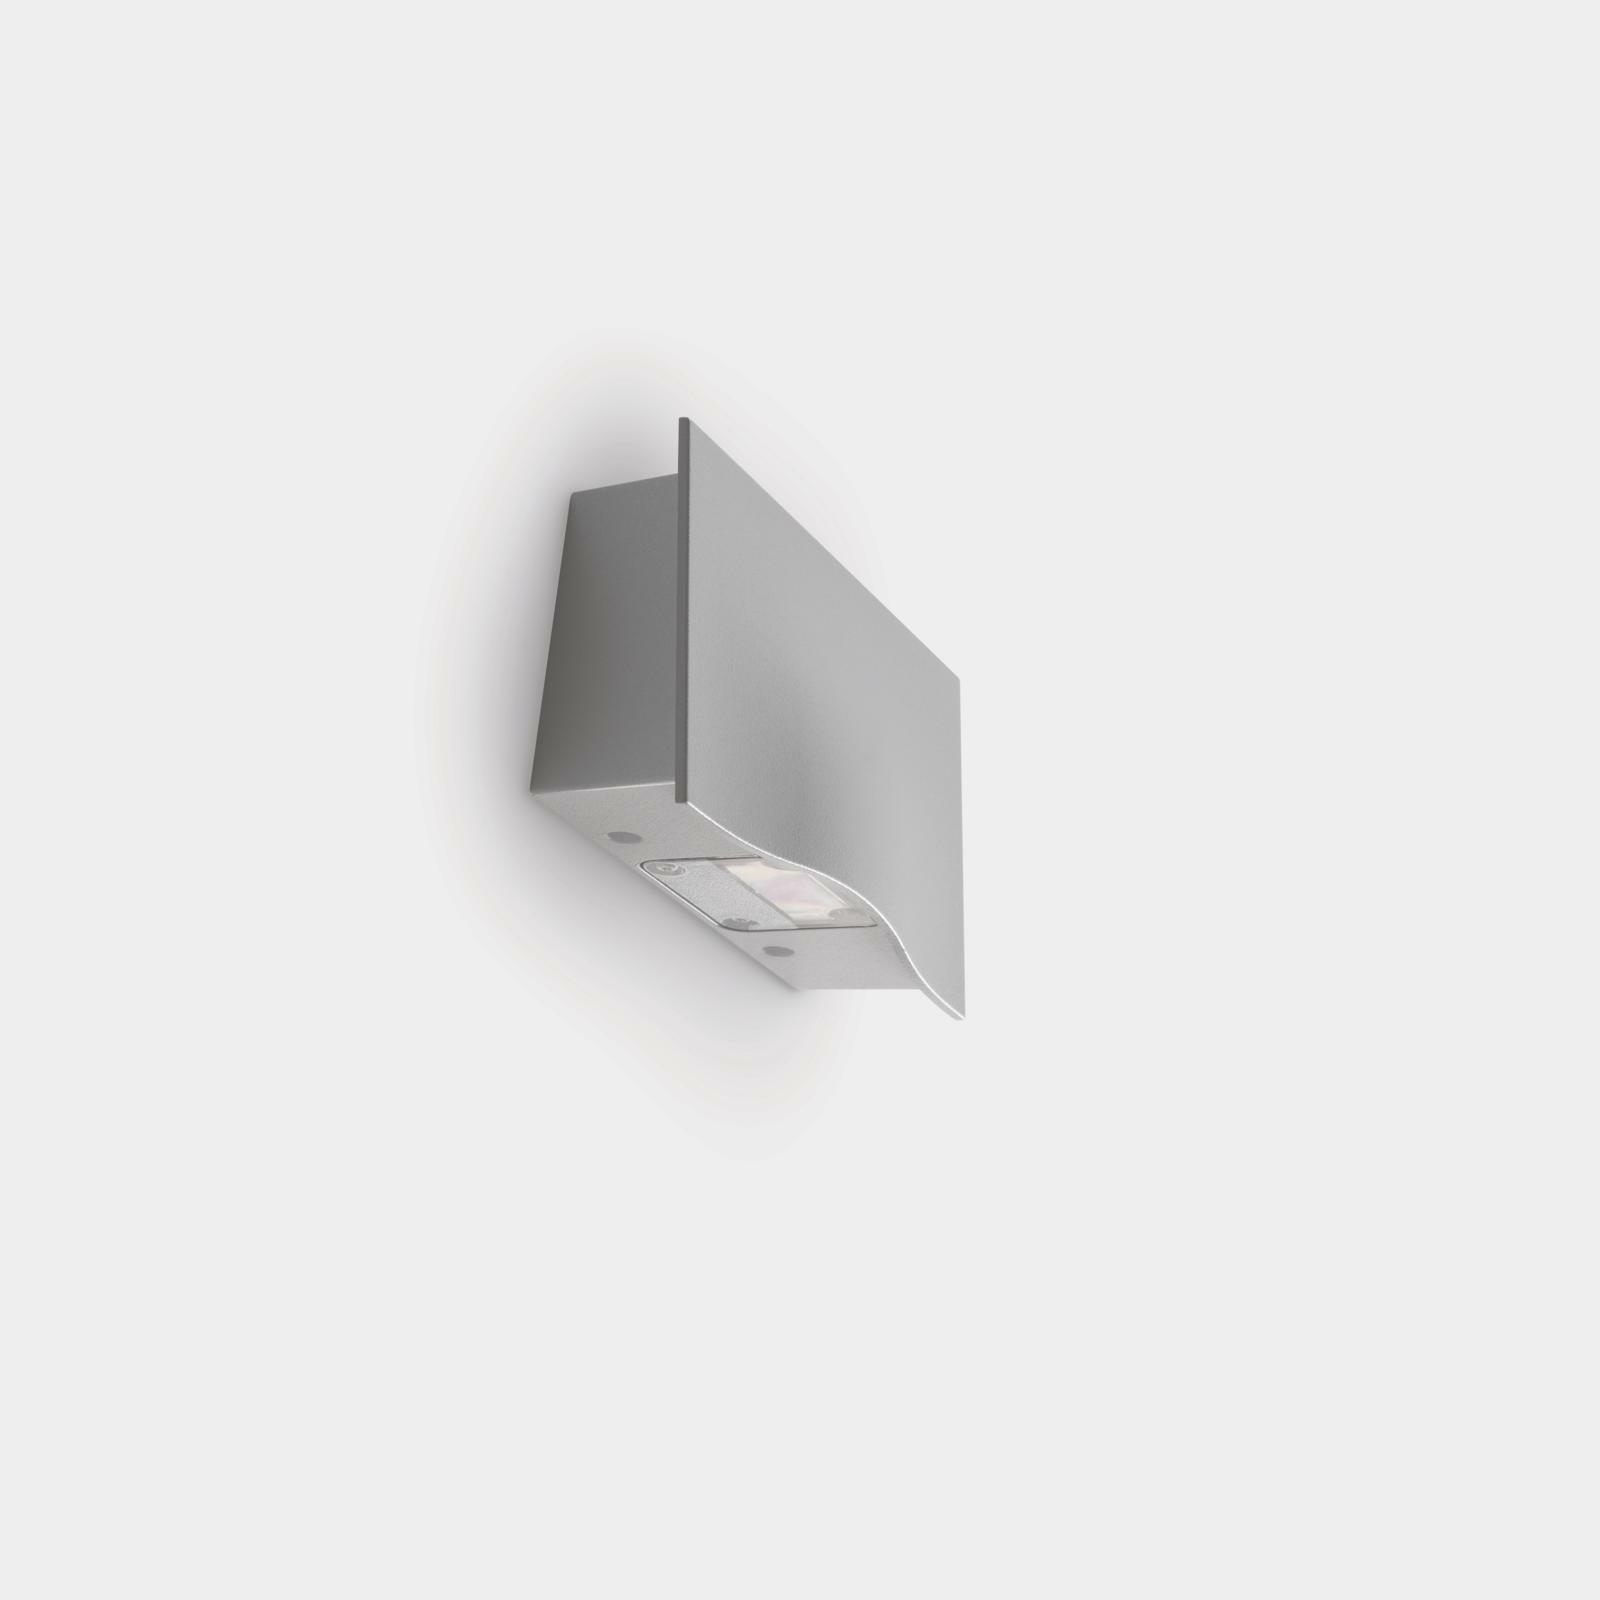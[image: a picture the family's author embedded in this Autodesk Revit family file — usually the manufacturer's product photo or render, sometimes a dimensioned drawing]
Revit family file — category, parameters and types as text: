
# Revit family: BALTI 80
name_source: partatom
category: Lighting Fixtures
units: mm (PartAtom-declared; Revit-internal decimal feet)

## family parameters
Cut with Voids When Loaded = No
Host = Face
Light Source = Yes
OmniClass Number = 23.80.70.11
OmniClass Title = Luminaries for Internal Lighting
Part Type = Normal
Room Calculation Point = No
Round Connector Dimension = Use Diameter
Shared = No

## types (2) — shared parameters
Beam angle (°) = 110°
CRI L'indice di Resa Cromatica = 85
Color Filter = 16777215
Description = Balti 80 è un'applique per esterni, progettata per LED COB di ultima generazione, a dissipazione termica passiva.
Il profilo estremamente aderente alla parete, lo rende ideale per applicazioni in aree di passaggio, terrazze e come luce da facciata.
Il fascio luminoso di Balti è stato studiato con un’apertura specifica che permette di illuminare ampiamente la parete e, a seconda dell’applicazione, il soffitto o il pavimento.
Pressacavo di ottone, alto grado di protezione IP65.
Grazie alla sua versatilità ed eleganza, Balti 80 trova soluzioni di impiego anche in interni.
Dimming Lamp Color Temperature Shift = <None>
Effective Intensity (lm) = 646
Height = 83 mm
Lamp = LED 850lm 6.5W 3000K CRI85
Larghezza = 153 mm
Manufacturer = ARIA
Model = 11930
Photometric Web File = BALTI 80.IES
Tilt Angle = 90.00°
Type Comments = Outdoor wall light
URL = https://www.aria.lighting
Wattage Comments = 6.5

## per-type parameters (varying)
| type | Body material | Codice | Type Image |
| Balti 80 6,5W 3000K CRI85 WHITE | White Powder Coated Aluminium | 119304 | BALTI 80 WHITE.jpg |
| Balti 80 6,5W 3000K CRI85 METAL | Aluminum | 119303 | BALTI 80 METAL.jpg |

## geometry (parser evidence)
native form markers: Sweep x3
no freeform markers — native parametric forms only
